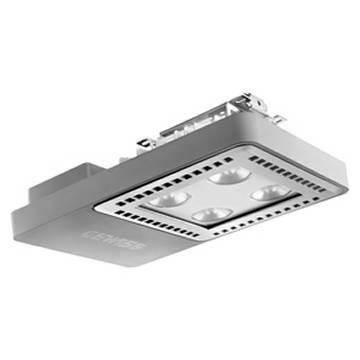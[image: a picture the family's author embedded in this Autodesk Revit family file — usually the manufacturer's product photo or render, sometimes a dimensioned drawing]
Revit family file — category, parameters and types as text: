
# Revit family: Lighting-Industrial-GEWISS-SMART[4]ATEX_HIGHBAYS-LED_1M
name_source: partatom
category: Apparecchi per illuminazione
units: mm (PartAtom-declared; Revit-internal decimal feet)

## family parameters
Basato su piano di lavoro = Sì
Condiviso = No
Numero OmniClass = 23.80.00.00
Punto di calcolo locali = No
Quota connettore circolare = Usa diametro
Sempre verticale = No
Sorgente d'illuminazione = No
Taglio con vuoti quando caricato = No
Tipo di parte = Normale
Titolo OmniClass = Electric Power and Lighting

## types (8) — shared parameters
Application = Internal
Body = PA6 "Halogen Free" loaded fibreglass
Carico apparente = 50 VA
Catalogue = LIGHTING
Classification: = ATEX: II 3 G Ex nR IIC T6 Gc - II 3 D Ex tc IIIC T65°C Dc
Classificazione = Lighting
Color Rendering Index = CRI-80
Colour = Grey RAL 7035
Colour : = Grey RAL 7035
Commenti sul wattaggio = 50W
Context = Logistics and industrial manufacturing lighting
Control System = ON / OFF
Control System : = ON / OFF
DIN 18032-3 certification = -
Device with reduced surface temperature = Yes
Distanza tot_plafoniera = 74 mm  [stored 0.242782 ft]
Driver = Included
Driver Box = Built-in
Electrocod = 2444
Eletrical and lighting features = -
External screw = Stainless steel
Fixing = -
Gasket = anti-aging silicone
General information = -
Glow Wire Test : = 850 °C
IDF = 2a3fb045-3361-4e3b-8c6c-ee987c541a88
IDT = b95782d405ee4ca1a3b4b3dc6b47d217
IP degree = IP66
IPEA = -
Immagine tipo = GWL1071.jpg
Installationa and maintenance = -
Insulation class = I
LED Maintenance = Non-replaceable
Lampada = LED
Larghezza = 253 mm  [stored 0.830052 ft]
Lifetime = L90B10 (Tq+25°C) = 100.000 h - L90B10 (Tq+40°C) = 50.000 h
Locking Hook = -
Luminaire = LED Industrial ReflectorÂ
Lunghezza = 383 mm  [stored 1.25656 ft]
Materials = -
Maximum surface exposed to the wind : = 0,097 m²
Motore = <Per categoria>
Mouting and installation = Ceiling - Wallmounting - Suspension
Operating temperature : = +5°C / +40 °C
Optic Maintenance = Non-replaceable
Optic and illuminating features = -
Overvoltage protection = DM 6 kV / CM 10 kV
Photobiological Risk Class = RG0
Plafoniera = <Per categoria>
Produttore = GEWISS S.p.A.
Prospetto di default = 1219 mm
Raggio led = 30 mm  [stored 0.0984252 ft]
Rated frequency (Hz) = 50/60 Hz
Shield type = Tempered glass Thickness 4mm
Shock resistance = IK08
Spessore plafoniera = 40 mm
Standard Deviation Colour Matching = SDCM = 3
Standard- = EN 60079-0 ; EN 60079-15 ; EN 60079-31 ; EN 60598-1 ; EN 60598-2-1
Standards and approvals = -
Stocking temperature = -40 +70 °C
Supply voltage = 220 - 240 V
System power = 64W
Technical sheet = https://www.gewiss.com
Tilt- = With bracket accessory
Trasformatore = <Per categoria>
Type of light source = LED - Not replaceable
URL = https://www.gewiss.com
Unique digital code (Datamatrix) = Datamatrix
Version file RFA = 20.11
Vetro acceso = Lampada accesa
Voltaggio = 230 V
Warranty = 5 years
Weight (kg): = 3,5
Wiring = Single wiring with anti-breathing cable exiting metallic PG (NO Connector)

## per-type parameters (varying)
| type | Colour temperature | Descrizione | Efficiency (lm/W) | Lumen output (lm) | Modello | Optic | Optic : | Unified Glare Rating |
| GWS4120FP857 - SMART4LB 1M ST.AL.ON/OFF ATEX 90° 57K | 5700K | SMART[4]LB 1M ST.AL.ON/OFF ATEX 90° 57K | 142 | 9100 | GWS4120FP857 | 90° | Metallic PC reflector and PMMA lenses | UGR - 25 |
| GWS4120FC857 - SMART4LB 1M ST.AL.ON/OFF ATEX ASI.57K | 5700K | SMART[4]LB 1M ST.AL.ON/OFF ATEX ASI.57K | 127 | 8100 | GWS4120FC857 | Asymmetrical | Metallic PC reflector and PMMA lenses | - |
| GWS4120FP840 - SMART4LB 1M ST.AL.ON/OFF ATEX 90° 40K | 4000K | SMART[4]LB 1M ST.AL.ON/OFF ATEX 90° 40K | 142 | 9100 | GWS4120FP840 | 90° | Metallic PC reflector and PMMA lenses | UGR - 25 |
| GWS4120FH857 - SMART4LB 1M ST.AL.ON/OFF ATEX 60° 57K | 5700K | SMART[4]LB 1M ST.AL.ON/OFF ATEX 60° 57K | 141 | 9000 | GWS4120FH857 | 60° | Metallic PC reflector and PMMA lenses | UGR - 25 |
| GWS4120FA857 - SMART4LB 1M ST.AL.ON/OFF ATEX ARR.57K | 5700K | SMART[4]LB 1M ST.AL.ON/OFF ATEX ARR.57K | 139 | 8900 | GWS4120FA857 | Array | Metallized polycarbonate reflector | - |
| GWS4120FA840 - SMART4LB 1M ST.AL.ON/OFF ATEX ARR.40K | 4000K | SMART[4]LB 1M ST.AL.ON/OFF ATEX ARR.40K | 139 | 8900 | GWS4120FA840 | Array | Metallized polycarbonate reflector | - |
| GWS4120FC840 - SMART4LB 1M ST.AL.ON/OFF ATEX ASI.40K | 4000K | SMART[4]LB 1M ST.AL.ON/OFF ATEX ASI.40K | 127 | 8100 | GWS4120FC840 | Asymmetrical | Metallic PC reflector and PMMA lenses | - |
| GWS4120FH840 - SMART4LB 1M ST.AL.ON/OFF ATEX 60° 40K | 4000K | SMART[4]LB 1M ST.AL.ON/OFF ATEX 60° 40K | 141 | 9000 | GWS4120FH840 | 60° | Metallic PC reflector and PMMA lenses | UGR - 25 |

note: [stored X ft] marks values corroborated as IEEE doubles in the binary element streams (Revit-internal decimal feet)

## geometry (parser evidence)
native form markers: Blend x4
no freeform markers — native parametric forms only
